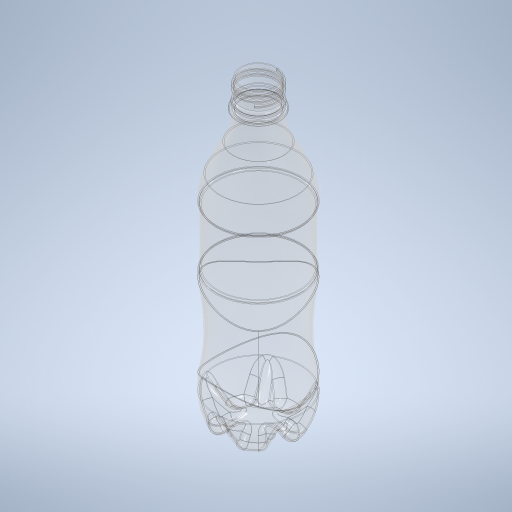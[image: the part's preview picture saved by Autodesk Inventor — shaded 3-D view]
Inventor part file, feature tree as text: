
AUTODESK INVENTOR PART (.ipt)
format: ipt  version: 2024 (Build 280153000, 153)  size: 1,616,896 bytes
history: native  units: mm
features: sketch x10, plane x5, other x3, revolve x2, extrude x2, sweep x2, fillet x2, loft x1, pattern_circular x1, shell x1
ambient origin geometry x8: Origin, YZ Plane, XZ Plane, XY Plane, X Axis, Y Axis, Z Axis, Center Point
bodies: Solid1 (feature_tree)
feature tree (29):
  sketch  "Sketch1"  dims[d0=215.0mm d1=15.0mm]
  revolve  "Revolution1"  [1 undecoded]
  extrude  "Extrusion1"  Depth=5.0mm
  plane  "Work Plane1"
  extrude  "Extrusion2"  Depth=40.0mm
  plane  "Work Plane2"
  loft  "Loft1"
  sketch  "Sketch6"  dims[d10=30.5mm d11=40.0mm d12=1.0mm d13=40.0mm d14=1.0mm d15=75.0mm]
  plane  "Work Plane3"
  sweep  "Sweep1"
  fillet  "Fillet1"  Radius=1.0mm
  pattern_circular  "Circular Pattern1"  Count=4  [1 undecoded]
  fillet  "Fillet2"  Radius=1.0mm
  shell  "Shell1"  Thickness=75.0mm
  revolve  "Revolution2"  [1 undecoded]
  plane  "Work Plane4"
  sketch  "3D Sketch1"
  plane  "Work Plane5"
  sweep  "Sweep2"
  sketch  "Sketch3"  dims[d4=0.5mm d5=5.0mm]
  sketch  "Sketch4"  dims[d6=18.0mm d7=40.0mm]
  sketch  "Sketch5"  dims[d8=27.5mm d9=200.0mm]
  other  "Edges1"
  other  "Edges2"
  sketch  "Sketch7"  dims[d16=7.5mm d17=40.0mm]
  sketch  "Sketch8"  dims[d18=6.0mm d19=25.0mm]
  sketch  "Sketch9"  dims[d24=12.5mm]
  other  "Helical Curve1"
  sketch  "Sketch10"  dims[d25=90.0deg d26=65.0mm d27=90.0mm d28=25.0mm d29=0.0mm d30=0.0mm d31=45.0deg d32=90.0mm d33=15.0mm d34=0.0mm d35=0.0mm d36=-155.0mm d37=55.0mm d38=0.0mm d39=90.0deg d40=0.0mm d41=90.0deg d42=0.0mm d43=90.0deg d44=20.0mm d45=21.380283mm d46=6.0mm d47=2.8mm d48=20.0mm d49=22.5deg d50=22.5deg d51=36.0mm d52=0.0mm d53=0.0mm d54=0.0mm d55=5.0mm d56=50.0mm d57=360.0deg d59=1.0mm d60=0.75mm d61=7.75mm d62=2.25mm d63=2.0mm d64=1.745329mm d65=1.0mm d66=0.5mm d67=0.5mm d68=1.0mm d69=1.7mm d70=90.0deg d71=-2.0mm d72=3.0mm d73=24.0mm d74=25.0mm d75=0.0mm d76=1.5mm d77=1.15mm d78=30.0deg d79=0.0mm d80=0.0mm]
note: 3 required parameter values undecoded (feature->parameter linkage not recoverable at this tier; creation-order binding heuristic only, values carry confidence <= 0.55)